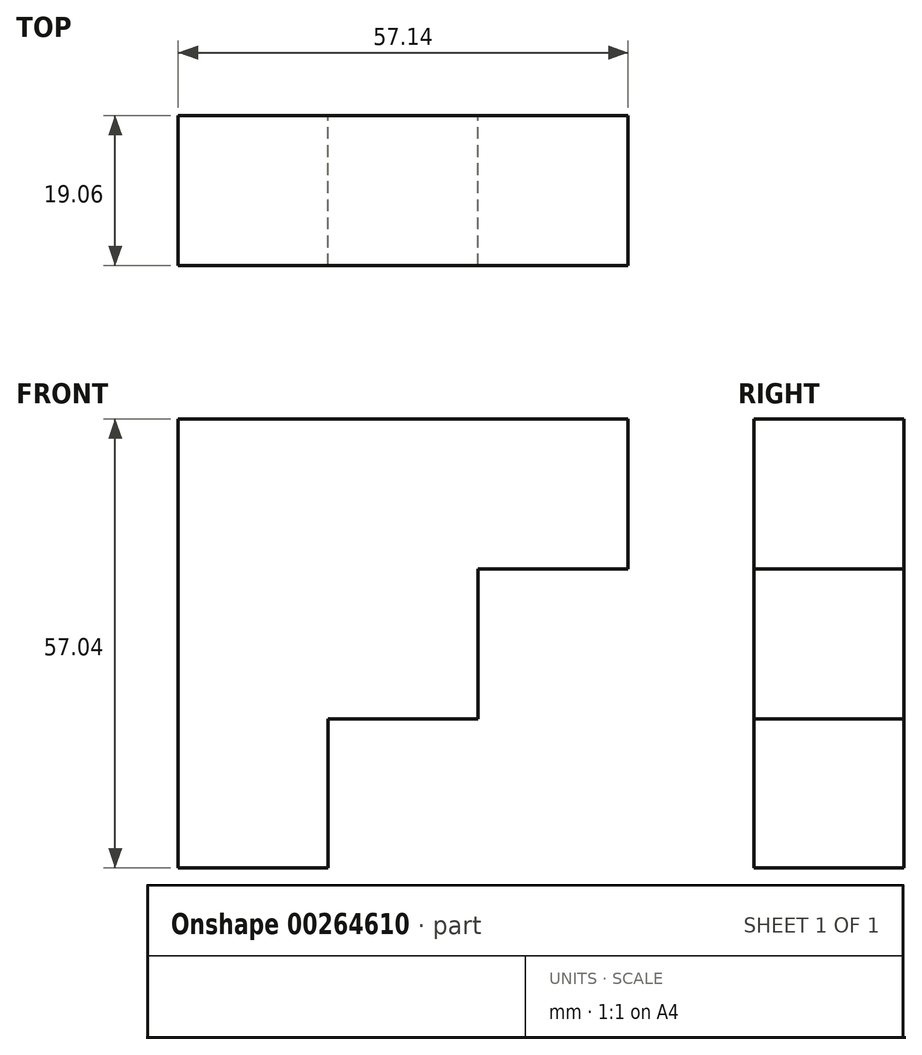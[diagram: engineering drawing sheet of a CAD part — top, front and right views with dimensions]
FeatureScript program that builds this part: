
annotation { "Feature Type Name" : "Feature", "Feature Type Description" : "" }
export const myFeature = defineFeature(function(context is Context, id is Id, definition is map)
    precondition{}
    {
        {
            var Q0;
            Q0=qCreatedBy(makeId("Front.planeOp"),FACE);
            var sketch = newSketch(context, id + "F0", { "sketchPlane" : qUnion([Q0])});
            skLineSegment(sketch, "E0.bottom", {"start": v(9.53, -9.52) * mm, "end": v(-9.52, -9.53) * mm});
            skLineSegment(sketch, "E0.top", {"start": v(9.52, 9.53) * mm, "end": v(-9.53, 9.53) * mm});
            skLineSegment(sketch, "E0.left", {"start": v(9.53, -9.52) * mm, "end": v(9.52, 9.53) * mm});
            skLineSegment(sketch, "E0.right", {"start": v(-9.52, -9.53) * mm, "end": v(-9.53, 9.53) * mm});
            skPoint(sketch, "E0.middle", {"position": v(0, 0) * mm});
            skLineSegment(sketch, "E1.bottom", {"start": v(9.52, 9.53) * mm, "end": v(-9.53, 9.52) * mm});
            skLineSegment(sketch, "E1.top", {"start": v(9.52, 28.57) * mm, "end": v(-9.53, 28.57) * mm});
            skLineSegment(sketch, "E1.left", {"start": v(9.52, 9.52) * mm, "end": v(9.52, 28.57) * mm});
            skLineSegment(sketch, "E1.right", {"start": v(-9.53, 9.52) * mm, "end": v(-9.53, 28.57) * mm});
            skPoint(sketch, "E1.middle", {"position": v(0, 19.05) * mm});
            skLineSegment(sketch, "E2.bottom", {"start": v(28.57, 9.53) * mm, "end": v(9.52, 9.53) * mm});
            skLineSegment(sketch, "E2.top", {"start": v(28.57, 28.58) * mm, "end": v(9.52, 28.58) * mm});
            skLineSegment(sketch, "E2.left", {"start": v(28.57, 9.53) * mm, "end": v(28.57, 28.58) * mm});
            skLineSegment(sketch, "E2.right", {"start": v(9.53, 9.53) * mm, "end": v(9.52, 28.58) * mm});
            skPoint(sketch, "E2.middle", {"position": v(19.05, 19.05) * mm});
            skLineSegment(sketch, "E3.bottom", {"start": v(-9.53, 9.53) * mm, "end": v(-28.57, 9.53) * mm});
            skLineSegment(sketch, "E3.top", {"start": v(-9.52, -9.42) * mm, "end": v(-28.57, -9.42) * mm});
            skLineSegment(sketch, "E3.left", {"start": v(-9.53, 9.52) * mm, "end": v(-9.53, -9.42) * mm});
            skLineSegment(sketch, "E3.right", {"start": v(-28.57, 9.52) * mm, "end": v(-28.57, -9.42) * mm});
            skLineSegment(sketch, "E4.bottom", {"start": v(-9.53, 28.57) * mm, "end": v(-28.57, 28.57) * mm});
            skLineSegment(sketch, "E4.left", {"start": v(-9.53, 28.57) * mm, "end": v(-9.53, 9.53) * mm});
            skLineSegment(sketch, "E4.right", {"start": v(-28.57, 28.57) * mm, "end": v(-28.57, 9.52) * mm});
            skLineSegment(sketch, "E5.top", {"start": v(-9.53, -28.47) * mm, "end": v(-28.57, -28.47) * mm});
            skLineSegment(sketch, "E5.left", {"start": v(-9.53, -9.42) * mm, "end": v(-9.53, -28.47) * mm});
            skLineSegment(sketch, "E5.right", {"start": v(-28.57, -9.42) * mm, "end": v(-28.57, -28.47) * mm});
            skSolve(sketch);
        }
        {
            var Q0;
            Q0 = qSketchRegion(id + "F0", true);
            extrude(context, id + "F1", {"entities" : qUnion([Q0]), "endBound" : BoundingType.SYMMETRIC, "depth" : 19.05 * mm});
        }
    });
